# Revit family: Air-Curtain_Climate-Control_PoweredAire_ETD
name_source: partatom
category: Mechanical Equipment
revit_build: Autodesk Revit 2016 (Build: 20150714_1515(x64)
units: mm (PartAtom-declared; Revit-internal decimal feet)

## family parameters
Cut with Voids When Loaded = No
Host = Face
OmniClass Number = 23.75.35.17.21
OmniClass Title = Air Curtains
Part Type = Normal
Room Calculation Point = No
Round Connector Dimension = Use Diameter
Shared = No

## types (1)
- Air-Curtain_Climate-Control_PoweredAire_ETD
    Assembly Code = D3090400
    Construction Details = http://www.arcat.com
    Default Elevation = 0' - 0"
    Description = Powered Aire Air Curtain as Specified
    Expected Lifespan (Years) = 0
    Green Building-LEED = http://www.arcat.com
    HVAC_Outlet Velocity Uniformity = 0
    Heating Element Load = 0 W
    Keynote = 23 34 33
    Maintenance Schedule (Months) = 0
    Manufacturer = Powered Aire, Inc
    Manufacturer Fax = 724-588-3371
    Manufacturer Website = http://www.poweredaire.com
    Max Height = 0' - 0"
    Model = As Specified
    Motor Count = 0
    Motor HP = 0
    Motor RPM = 0
    Mounting Width = 2' - 11 1/16"
    Nozzle Width = 2' - 11"
    Outlet Velocity_Range = as Specified
    Outlet Volume_Range = as Specified
    Power Rating = 0 W
    Product Data = http://www.arcat.com
    Revision = R1_2016-08
    Sales Information = http://www.poweredaire.com
    Sound Pressure = as Specified
    Specification = http://www.arcat.com
    Standards Conformance = as Specified
    Temperature Rise_Range = as Specified
    URL = http://www.poweredaire.com
    Unit Depth = 1' - 5 1/2"
    Unit Height = 1' - 3"
    Unit Weight = 0
    Unit Width = 3' - 0"
    Unit Width Notes = Other Widths available.
    Warranty Duration (Years) = 0

## geometry (parser evidence)
native form markers: Blend x8, Sweep x1
no freeform markers — native parametric forms only
